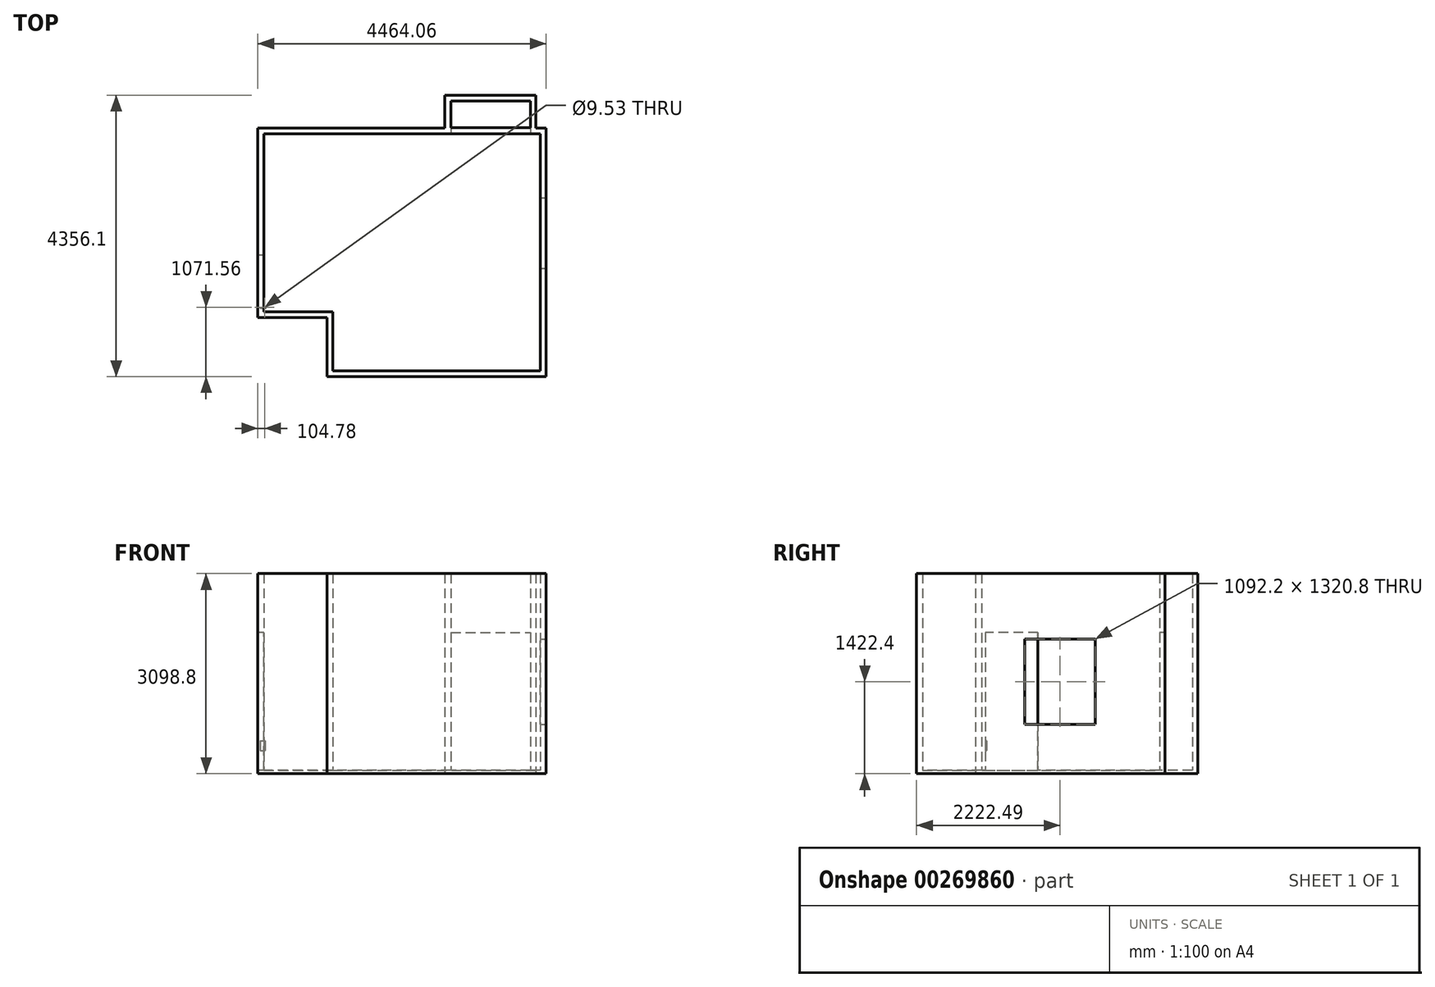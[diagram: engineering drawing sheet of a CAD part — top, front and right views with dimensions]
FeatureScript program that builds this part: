
annotation { "Feature Type Name" : "Feature", "Feature Type Description" : "" }
export const myFeature = defineFeature(function(context is Context, id is Id, definition is map)
    precondition{}
    {
        {
            var Q0;
            Q0=qCreatedBy(makeId("Top.planeOp"),FACE);
            var sketch = newSketch(context, id + "F0", { "sketchPlane" : qUnion([Q0])});
            skLineSegment(sketch, "E0", {"start": v(-2133.6, 1828.8) * mm, "end": v(-2133.6, -914.4) * mm});
            skLineSegment(sketch, "E1", {"start": v(-1066.8, -914.4) * mm, "end": v(-1066.8, -1828.8) * mm});
            skLineSegment(sketch, "E2", {"start": v(-2133.6, -914.4) * mm, "end": v(-1066.8, -914.4) * mm});
            skLineSegment(sketch, "E3", {"start": v(-1066.8, -1828.8) * mm, "end": v(2133.6, -1828.8) * mm});
            skLineSegment(sketch, "E4", {"start": v(2133.6, -1828.8) * mm, "end": v(2133.6, 1828.8) * mm});
            skLineSegment(sketch, "E5", {"start": v(2133.6, 1828.8) * mm, "end": v(1981.2, 1828.8) * mm});
            skLineSegment(sketch, "E6", {"start": v(1981.2, 1828.8) * mm, "end": v(1981.2, 2336.8) * mm});
            skLineSegment(sketch, "E7", {"start": v(1981.2, 2336.8) * mm, "end": v(762, 2336.8) * mm});
            skLineSegment(sketch, "E8", {"start": v(762, 2336.8) * mm, "end": v(762, 1828.8) * mm});
            skLineSegment(sketch, "E9", {"start": v(762, 1828.8) * mm, "end": v(-2133.6, 1828.8) * mm});
            skLineSegment(sketch, "E10.0", {"start": v(755.65, 1835.15) * mm, "end": v(-2139.95, 1835.15) * mm});
            skLineSegment(sketch, "E10.1", {"start": v(755.65, 2343.15) * mm, "end": v(755.65, 1835.15) * mm});
            skLineSegment(sketch, "E10.2", {"start": v(-2139.95, 1835.15) * mm, "end": v(-2139.95, -920.75) * mm});
            skLineSegment(sketch, "E10.3", {"start": v(1987.55, 2343.15) * mm, "end": v(755.65, 2343.15) * mm});
            skLineSegment(sketch, "E10.4", {"start": v(1987.55, 1835.15) * mm, "end": v(1987.55, 2343.15) * mm});
            skLineSegment(sketch, "E10.5", {"start": v(2139.95, 1835.15) * mm, "end": v(1987.55, 1835.15) * mm});
            skLineSegment(sketch, "E10.6", {"start": v(-2139.95, -920.75) * mm, "end": v(-1073.15, -920.75) * mm});
            skLineSegment(sketch, "E10.7", {"start": v(-1073.15, -920.75) * mm, "end": v(-1073.15, -1835.15) * mm});
            skLineSegment(sketch, "E10.8", {"start": v(-1073.15, -1835.15) * mm, "end": v(2139.95, -1835.15) * mm});
            skLineSegment(sketch, "E10.9", {"start": v(2139.95, -1835.15) * mm, "end": v(2139.95, 1835.15) * mm});
            skLineSegment(sketch, "E11.0", {"start": v(663.58, 1920.88) * mm, "end": v(-2232.03, 1920.87) * mm});
            skLineSegment(sketch, "E12.0", {"start": v(663.58, 2428.88) * mm, "end": v(663.58, 1920.88) * mm});
            skLineSegment(sketch, "E13.0", {"start": v(2073.28, 2428.88) * mm, "end": v(663.58, 2428.88) * mm});
            skLineSegment(sketch, "E14.0", {"start": v(2073.28, 1920.87) * mm, "end": v(2073.28, 2428.88) * mm});
            skLineSegment(sketch, "E15", {"start": v(2073.28, 1920.87) * mm, "end": v(2232.02, 1920.87) * mm});
            skLineSegment(sketch, "E16", {"start": v(2232.02, 1920.87) * mm, "end": v(2232.03, -1927.22) * mm});
            skLineSegment(sketch, "E17", {"start": v(2232.03, -1927.22) * mm, "end": v(-1158.87, -1927.23) * mm});
            skLineSegment(sketch, "E18", {"start": v(-1158.87, -1927.23) * mm, "end": v(-1158.87, -1012.83) * mm});
            skLineSegment(sketch, "E19", {"start": v(-1158.87, -1012.83) * mm, "end": v(-2232.02, -1012.83) * mm});
            skLineSegment(sketch, "E20", {"start": v(-2232.02, -1012.83) * mm, "end": v(-2232.03, 1920.87) * mm});
            skSolve(sketch);
        }
        {
            var Q0;
            Q0 = qSketchRegion(id + "F0", true);
            var Q1;
            Q1=sQuery(id+"F0.wireOp",EDGE,"E0");
            var Q2;
            Q2=sQuery(id+"F0.wireOp",EDGE,"E9");
            var Q3;
            Q3=sQuery(id+"F0.wireOp",EDGE,"E8");
            var Q4;
            Q4=sQuery(id+"F0.wireOp",EDGE,"E7");
            var Q5;
            Q5=sQuery(id+"F0.wireOp",EDGE,"E6");
            var Q6;
            Q6=sQuery(id+"F0.wireOp",EDGE,"E5");
            var Q7;
            Q7=sQuery(id+"F0.wireOp",EDGE,"E4");
            var Q8;
            Q8=sQuery(id+"F0.wireOp",EDGE,"E3");
            var Q9;
            Q9=sQuery(id+"F0.wireOp",EDGE,"E1");
            var Q10;
            Q10=sQuery(id+"F0.wireOp",EDGE,"E2");
            extrude(context, id + "F1", {"entities" : qUnion([Q0]), "surfaceEntities" : qUnion([Q1, Q2, Q3, Q4, Q5, Q6, Q7, Q8, Q9, Q10]), "depth" : 3048 * mm});
        }
        {
            var Q0;
            Q0=makeQuery(id+"F1.opExtrude","SWEPT_FACE",FACE,{"disambiguationData":[OSD([sQuery(id+"F0.wireOp",EDGE,"E16")])]});
            var sketch = newSketch(context, id + "F2", { "sketchPlane" : qUnion([Q0])});
            skLineSegment(sketch, "E21.bottom", {"start": v(-250.82, 2032) * mm, "end": v(841.38, 2032) * mm});
            skLineSegment(sketch, "E21.top", {"start": v(-250.82, 711.2) * mm, "end": v(841.38, 711.2) * mm});
            skLineSegment(sketch, "E21.left", {"start": v(-250.82, 2032) * mm, "end": v(-250.82, 711.2) * mm});
            skLineSegment(sketch, "E21.right", {"start": v(841.38, 2032) * mm, "end": v(841.38, 711.2) * mm});
            skSolve(sketch);
        }
        {
            var Q0;
            Q0=makeQuery(id+"F2.imprint","IMPRINT",FACE,{"disambiguationData":[TD([[makeQuery(id+"F2.imprint","IMPRINT",EDGE,{"derivedFrom":sQuery(id+"F2.wireOp",EDGE,"E21.bottom")}),-1.0]])]});
            extrude(context, id + "F3", {"entities" : qUnion([Q0]), "operationType" : NewBodyOperationType.REMOVE, "oppositeDirection" : true, "depth" : 101.6 * mm});
        }
        {
            var Q0;
            Q0=makeQuery(id+"F1.opExtrude","SWEPT_FACE",FACE,{"disambiguationData":[OSD([sQuery(id+"F0.wireOp",EDGE,"E20")])]});
            var sketch = newSketch(context, id + "F4", { "sketchPlane" : qUnion([Q0])});
            skLineSegment(sketch, "E22.bottom", {"start": v(47.63, 2133.6) * mm, "end": v(860.43, 2133.6) * mm});
            skLineSegment(sketch, "E22.top", {"start": v(47.63, 0) * mm, "end": v(860.43, 0) * mm});
            skLineSegment(sketch, "E22.left", {"start": v(47.63, 2133.6) * mm, "end": v(47.63, 0) * mm});
            skLineSegment(sketch, "E22.right", {"start": v(860.43, 2133.6) * mm, "end": v(860.43, 0) * mm});
            skSolve(sketch);
        }
        {
            var Q0;
            Q0=makeQuery(id+"F4.imprint","IMPRINT",FACE,{"disambiguationData":[TD([[makeQuery(id+"F4.imprint","IMPRINT",EDGE,{"derivedFrom":sQuery(id+"F4.wireOp",EDGE,"E22.bottom")}),-1.0]])]});
            extrude(context, id + "F5", {"entities" : qUnion([Q0]), "operationType" : NewBodyOperationType.REMOVE, "oppositeDirection" : true, "depth" : 101.6 * mm});
        }
        {
            var Q0;
            Q0=makeQuery(id+"F1.opExtrude","CAP_FACE",FACE,{"disambiguationData":[OSD([sQuery(id+"F0.wireOp",EDGE,"E10.0"),sQuery(id+"F0.wireOp",EDGE,"E10.1"),sQuery(id+"F0.wireOp",EDGE,"E10.2"),sQuery(id+"F0.wireOp",EDGE,"E10.3"),sQuery(id+"F0.wireOp",EDGE,"E10.4"),sQuery(id+"F0.wireOp",EDGE,"E10.5"),sQuery(id+"F0.wireOp",EDGE,"E10.6"),sQuery(id+"F0.wireOp",EDGE,"E10.7"),sQuery(id+"F0.wireOp",EDGE,"E10.8"),sQuery(id+"F0.wireOp",EDGE,"E10.9"),sQuery(id+"F0.wireOp",EDGE,"E11.0"),sQuery(id+"F0.wireOp",EDGE,"E12.0"),sQuery(id+"F0.wireOp",EDGE,"E13.0"),sQuery(id+"F0.wireOp",EDGE,"E14.0"),sQuery(id+"F0.wireOp",EDGE,"E15"),sQuery(id+"F0.wireOp",EDGE,"E16"),sQuery(id+"F0.wireOp",EDGE,"E17"),sQuery(id+"F0.wireOp",EDGE,"E18"),sQuery(id+"F0.wireOp",EDGE,"E19"),sQuery(id+"F0.wireOp",EDGE,"E20")])],"isStart":true});
            var sketch = newSketch(context, id + "F6", { "sketchPlane" : qUnion([Q0])});
            skLineSegment(sketch, "E23", {"start": v(-2232.02, 1012.83) * mm, "end": v(-2232.03, -1920.87) * mm});
            skLineSegment(sketch, "E24", {"start": v(-2232.03, -1920.87) * mm, "end": v(663.58, -1920.88) * mm});
            skLineSegment(sketch, "E25", {"start": v(663.58, -1920.88) * mm, "end": v(663.58, -2428.88) * mm});
            skLineSegment(sketch, "E26", {"start": v(663.58, -2428.88) * mm, "end": v(2073.28, -2428.88) * mm});
            skLineSegment(sketch, "E27", {"start": v(2073.28, -2428.88) * mm, "end": v(2073.28, -1920.87) * mm});
            skLineSegment(sketch, "E28", {"start": v(2073.28, -1920.87) * mm, "end": v(2232.02, -1920.87) * mm});
            skLineSegment(sketch, "E29", {"start": v(2232.02, -1920.87) * mm, "end": v(2232.03, 1927.22) * mm});
            skLineSegment(sketch, "E30", {"start": v(2232.03, 1927.22) * mm, "end": v(-1158.87, 1927.23) * mm});
            skLineSegment(sketch, "E31", {"start": v(-1158.87, 1927.23) * mm, "end": v(-1158.87, 1012.83) * mm});
            skLineSegment(sketch, "E32", {"start": v(-1158.87, 1012.83) * mm, "end": v(-2232.02, 1012.83) * mm});
            skSolve(sketch);
        }
        {
            var Q0;
            {var subQ16=sQuery(id+"F6.wireOp",EDGE,"E24");Q0=makeQuery(id+"F6.imprint","IMPRINT",FACE,{"disambiguationData":[TD([[makeQuery(id+"F6.imprint","IMPRINT",EDGE,{"derivedFrom":subQ16}),-1.0]])]});}
            var Q1;
            {var subQ12=sQuery(id+"F0.wireOp",EDGE,"E10.0");Q1=makeQuery(id+"F6.imprint","IMPRINT",FACE,{"disambiguationData":[TD([[makeQuery(id+"F6.imprint","IMPRINT",EDGE,{"derivedFrom":makeQuery(id+"F1.opExtrude","CAP_EDGE",EDGE,{"disambiguationData":[OSD([subQ12])],"isStart":true})}),-1.0]])]});}
            extrude(context, id + "F7", {"entities" : qUnion([Q0, Q1]), "operationType" : NewBodyOperationType.ADD, "depth" : 50.8 * mm});
        }
        {
            var Q0;
            Q0=makeQuery(id+"F1.opExtrude","SWEPT_FACE",FACE,{"disambiguationData":[OSD([sQuery(id+"F0.wireOp",EDGE,"E10.0")])]});
            var sketch = newSketch(context, id + "F8", { "sketchPlane" : qUnion([Q0])});
            skLineSegment(sketch, "E33.bottom", {"start": v(755.65, 3048) * mm, "end": v(1987.55, 3048) * mm});
            skLineSegment(sketch, "E33.top", {"start": v(755.65, 2133.6) * mm, "end": v(1987.55, 2133.6) * mm});
            skLineSegment(sketch, "E33.left", {"start": v(755.65, 3048) * mm, "end": v(755.65, 2133.6) * mm});
            skLineSegment(sketch, "E33.right", {"start": v(1987.55, 3048) * mm, "end": v(1987.55, 2133.6) * mm});
            skSolve(sketch);
        }
        {
            var Q0;
            Q0=makeQuery(id+"F8.imprint","IMPRINT",FACE,{"disambiguationData":[TD([[makeQuery(id+"F8.imprint","IMPRINT",EDGE,{"derivedFrom":sQuery(id+"F8.wireOp",EDGE,"E33.bottom")}),-1.0]])]});
            extrude(context, id + "F9", {"entities" : qUnion([Q0]), "operationType" : NewBodyOperationType.ADD, "oppositeDirection" : true, "depth" : 92.07 * mm});
        }
        {
            var Q0;
            Q0=makeQuery(id+"F7.opExtrude","CAP_FACE",FACE,{"disambiguationData":[OSD([sQuery(id+"F6.wireOp",EDGE,"E23"),sQuery(id+"F6.wireOp",EDGE,"E24"),sQuery(id+"F6.wireOp",EDGE,"E25"),sQuery(id+"F6.wireOp",EDGE,"E26"),sQuery(id+"F6.wireOp",EDGE,"E27"),sQuery(id+"F6.wireOp",EDGE,"E28"),sQuery(id+"F6.wireOp",EDGE,"E29"),sQuery(id+"F6.wireOp",EDGE,"E30"),sQuery(id+"F6.wireOp",EDGE,"E31"),sQuery(id+"F6.wireOp",EDGE,"E32")])],"isStart":true});
            cPlane(context, id + "F10", {"entities" : qUnion([Q0]), "cplaneType" : CPlaneType.OFFSET, "offset" : 304.8 * mm, "width" : 152.4 * mm, "height" : 152.4 * mm});
        }
        {
            var Q0;
            Q0=qCreatedBy(id+"F10.planeOp",FACE);
            var sketch = newSketch(context, id + "F11", { "sketchPlane" : qUnion([Q0])});
            skLineSegment(sketch, "E34", {"start": v(-2197.1, -865.19) * mm, "end": v(-2127.25, -865.19) * mm});
            skLineSegment(sketch, "E35", {"start": v(-2197.1, -865.19) * mm, "end": v(-2197.1, -860.43) * mm});
            skLineSegment(sketch, "E36", {"start": v(-2197.1, -860.43) * mm, "end": v(-2135.5, -860.43) * mm});
            skArc(sketch, "E37", {"start": v(-2127.25, -865.19) * mm, "mid": v(-2122.49, -847.41) * mm, "end": v(-2135.5, -860.43) * mm});
            skCircle(sketch, "E38", {"center": v(-2127.25, -855.66) * mm, "radius": 4.76 * mm});
            skSolve(sketch);
        }
        {
            var Q0;
            Q0 = qSketchRegion(id + "F11", true);
            extrude(context, id + "F12", {"entities" : qUnion([Q0]), "depth" : 152.4 * mm});
        }
    });
